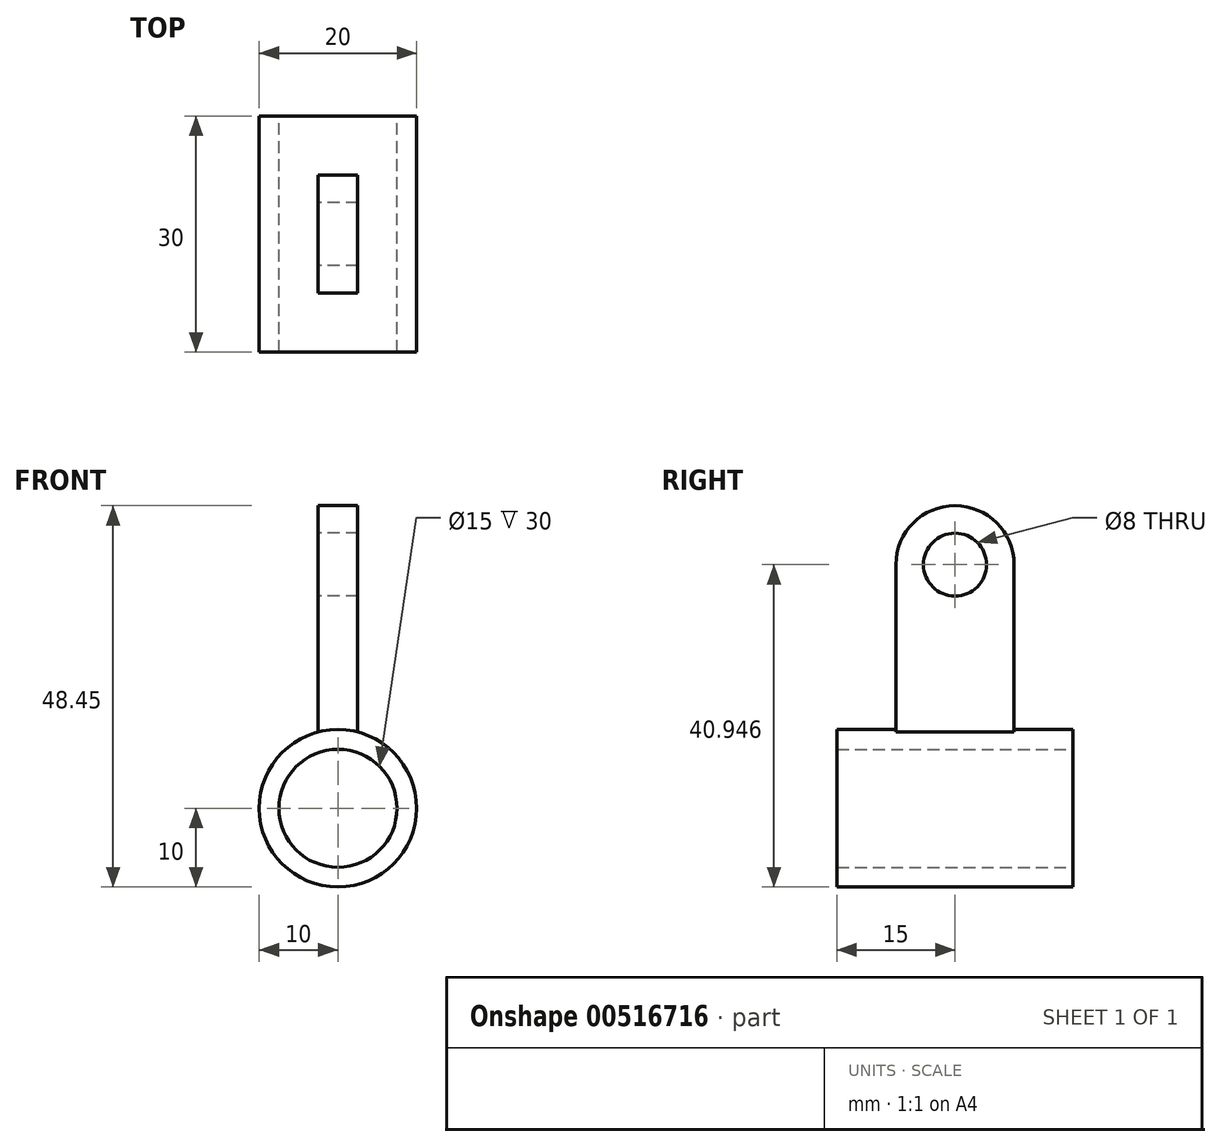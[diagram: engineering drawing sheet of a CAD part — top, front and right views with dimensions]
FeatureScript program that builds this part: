
annotation { "Feature Type Name" : "Feature", "Feature Type Description" : "" }
export const myFeature = defineFeature(function(context is Context, id is Id, definition is map)
    precondition{}
    {
        {
            var Q0;
            Q0=qCreatedBy(makeId("Front.planeOp"),FACE);
            var sketch = newSketch(context, id + "F0", { "sketchPlane" : qUnion([Q0])});
            skCircle(sketch, "E0", {"center": v(0, 0) * mm, "radius": 10 * mm});
            skCircle(sketch, "E1", {"center": v(0, 0) * mm, "radius": 7.5 * mm});
            skSolve(sketch);
        }
        {
            var Q0;
            Q0=makeQuery(id+"F0.imprint","IMPRINT",FACE,{"disambiguationData":[TD([[makeQuery(id+"F0.imprint","IMPRINT",EDGE,{"derivedFrom":sQuery(id+"F0.wireOp",EDGE,"E0")}),1.0]])]});
            extrude(context, id + "F1", {"entities" : qUnion([Q0]), "depth" : 30 * mm, "offsetDistance" : 25.4 * mm});
        }
        {
            var Q0;
            Q0=qCreatedBy(makeId("Right.planeOp"),FACE);
            var sketch = newSketch(context, id + "F2", { "sketchPlane" : qUnion([Q0])});
            skLineSegment(sketch, "E2.top", {"start": v(-7.5, 0.95) * mm, "end": v(-22.5, 0.95) * mm});
            skLineSegment(sketch, "E2.left", {"start": v(-7.5, 30.95) * mm, "end": v(-7.5, 0.95) * mm});
            skLineSegment(sketch, "E2.right", {"start": v(-22.5, 30.95) * mm, "end": v(-22.5, 0.95) * mm});
            skPoint(sketch, "E2.middle", {"position": v(-15, 15.95) * mm});
            skArc(sketch, "E3", {"start": v(-7.5, 30.95) * mm, "mid": v(-15, 38.45) * mm, "end": v(-22.5, 30.95) * mm});
            skCircle(sketch, "E4", {"center": v(-15, 30.95) * mm, "radius": 4 * mm});
            skLineSegment(sketch, "E5.bottom", {"start": v(-22.5, 0.95) * mm, "end": v(-7.5, 0.95) * mm});
            skLineSegment(sketch, "E5.left", {"start": v(-22.5, 0.95) * mm, "end": v(-22.5, -29.05) * mm});
            skLineSegment(sketch, "E5.right", {"start": v(-7.5, 0.95) * mm, "end": v(-7.5, -29.05) * mm});
            skArc(sketch, "E6", {"start": v(-22.5, -29.05) * mm, "mid": v(-15, -36.55) * mm, "end": v(-7.5, -29.05) * mm});
            skCircle(sketch, "E7", {"center": v(-15, -29.05) * mm, "radius": 4 * mm});
            skSolve(sketch);
        }
        {
            var Q0;
            Q0=makeQuery(id+"F2.imprint","IMPRINT",FACE,{"disambiguationData":[TD([[makeQuery(id+"F2.imprint","IMPRINT",EDGE,{"derivedFrom":sQuery(id+"F2.wireOp",EDGE,"E2.left")}),-1.0]])]});
            var Q1;
            Q1=makeQuery(id+"F2.imprint","IMPRINT",FACE,{"disambiguationData":[TD([[makeQuery(id+"F2.imprint","IMPRINT",EDGE,{"derivedFrom":sQuery(id+"F2.wireOp",EDGE,"E5.bottom")}),-1.0]])]});
            extrude(context, id + "F3", {"entities" : qUnion([Q0, Q1]), "operationType" : NewBodyOperationType.ADD, "endBound" : BoundingType.SYMMETRIC, "depth" : 5 * mm, "offsetDistance" : 25.4 * mm});
        }
        {
            var Q0;
            Q0=makeQuery(id+"F1.opExtrude","CAP_FACE",FACE,{"disambiguationData":[OSD([sQuery(id+"F0.wireOp",EDGE,"E0"),sQuery(id+"F0.wireOp",EDGE,"E1")])],"isStart":false});
            var sketch = newSketch(context, id + "F4", { "sketchPlane" : qUnion([Q0])});
            skCircle(sketch, "E8", {"center": v(0, 0) * mm, "radius": 7.5 * mm});
            skSolve(sketch);
        }
        {
            var Q0;
            Q0=makeQuery(id+"F4.imprint","IMPRINT",FACE,{"disambiguationData":[TD([[makeQuery(id+"F4.imprint","IMPRINT",EDGE,{"derivedFrom":sQuery(id+"F4.wireOp",EDGE,"E8")}),1.0]])]});
            extrude(context, id + "F5", {"entities" : qUnion([Q0]), "operationType" : NewBodyOperationType.REMOVE, "endBound" : BoundingType.THROUGH_ALL, "oppositeDirection" : true, "depth" : 25.4 * mm, "offsetDistance" : 25.4 * mm});
        }
    });
